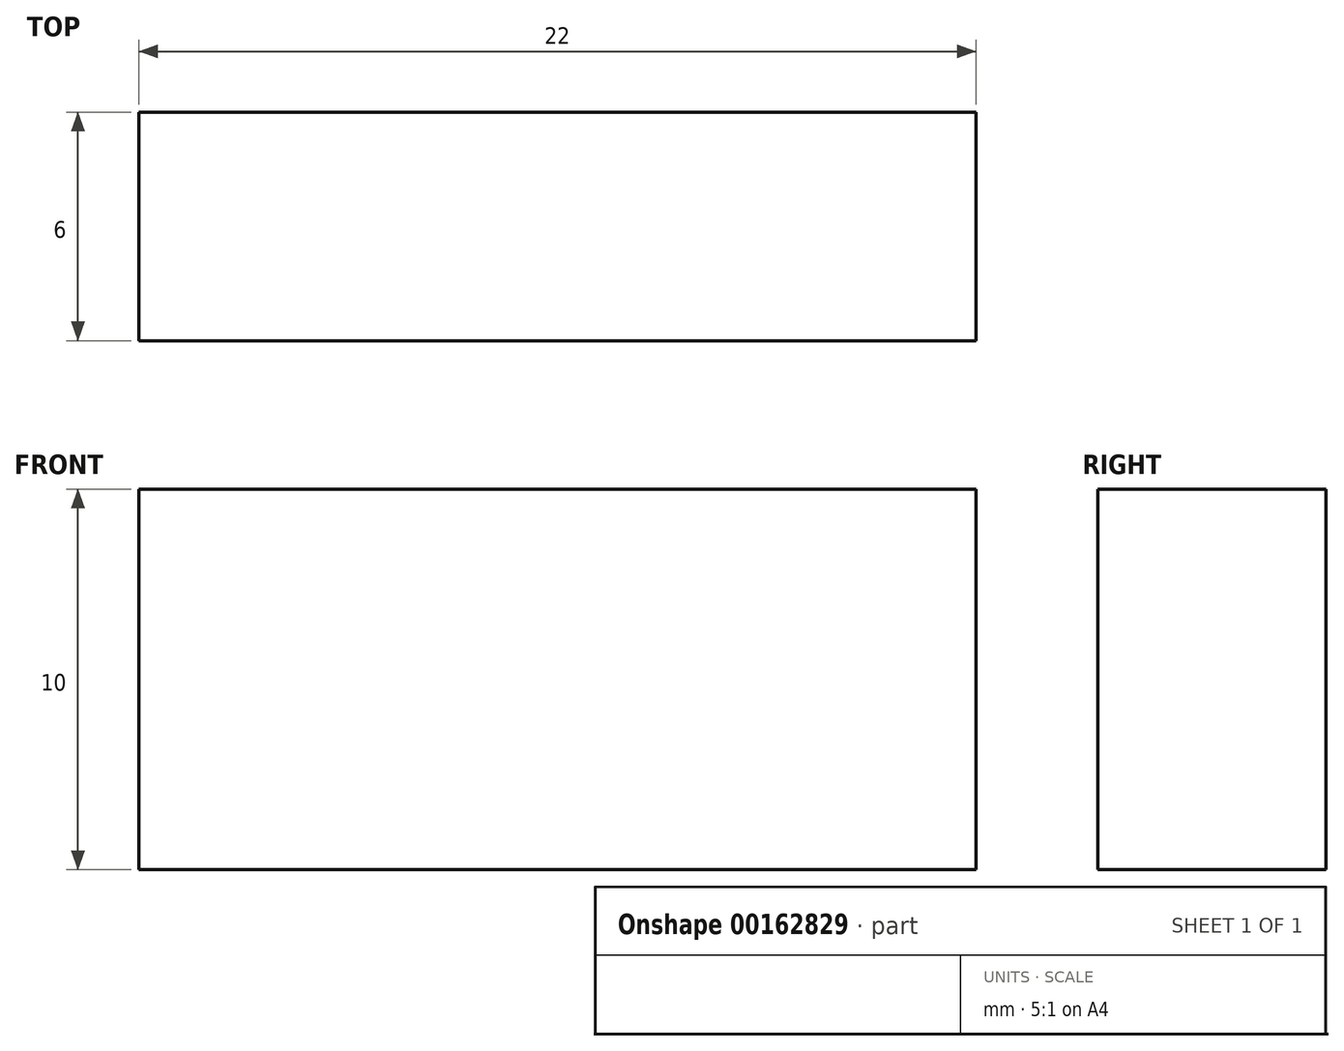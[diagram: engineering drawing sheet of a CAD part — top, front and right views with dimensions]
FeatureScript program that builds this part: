
annotation { "Feature Type Name" : "Feature", "Feature Type Description" : "" }
export const myFeature = defineFeature(function(context is Context, id is Id, definition is map)
    precondition{}
    {
        {
            var Q0;
            Q0=qCreatedBy(makeId("Top.planeOp"),FACE);
            var sketch = newSketch(context, id + "F0", { "sketchPlane" : qUnion([Q0])});
            skLineSegment(sketch, "E0.bottom", {"start": v(11, 3) * mm, "end": v(-11, 3) * mm});
            skLineSegment(sketch, "E0.top", {"start": v(11, -3) * mm, "end": v(-11, -3) * mm});
            skLineSegment(sketch, "E0.left", {"start": v(11, 3) * mm, "end": v(11, -3) * mm});
            skLineSegment(sketch, "E0.right", {"start": v(-11, 3) * mm, "end": v(-11, -3) * mm});
            skPoint(sketch, "E0.middle", {"position": v(0, 0) * mm});
            skSolve(sketch);
        }
        {
            var Q0;
            Q0=makeQuery(id+"F0.imprint","IMPRINT",FACE,{"disambiguationData":[TD([[makeQuery(id+"F0.imprint","IMPRINT",EDGE,{"derivedFrom":sQuery(id+"F0.wireOp",EDGE,"E0.bottom")}),1.0]])]});
            extrude(context, id + "F1", {"entities" : qUnion([Q0]), "depth" : 10 * mm});
        }
    });
